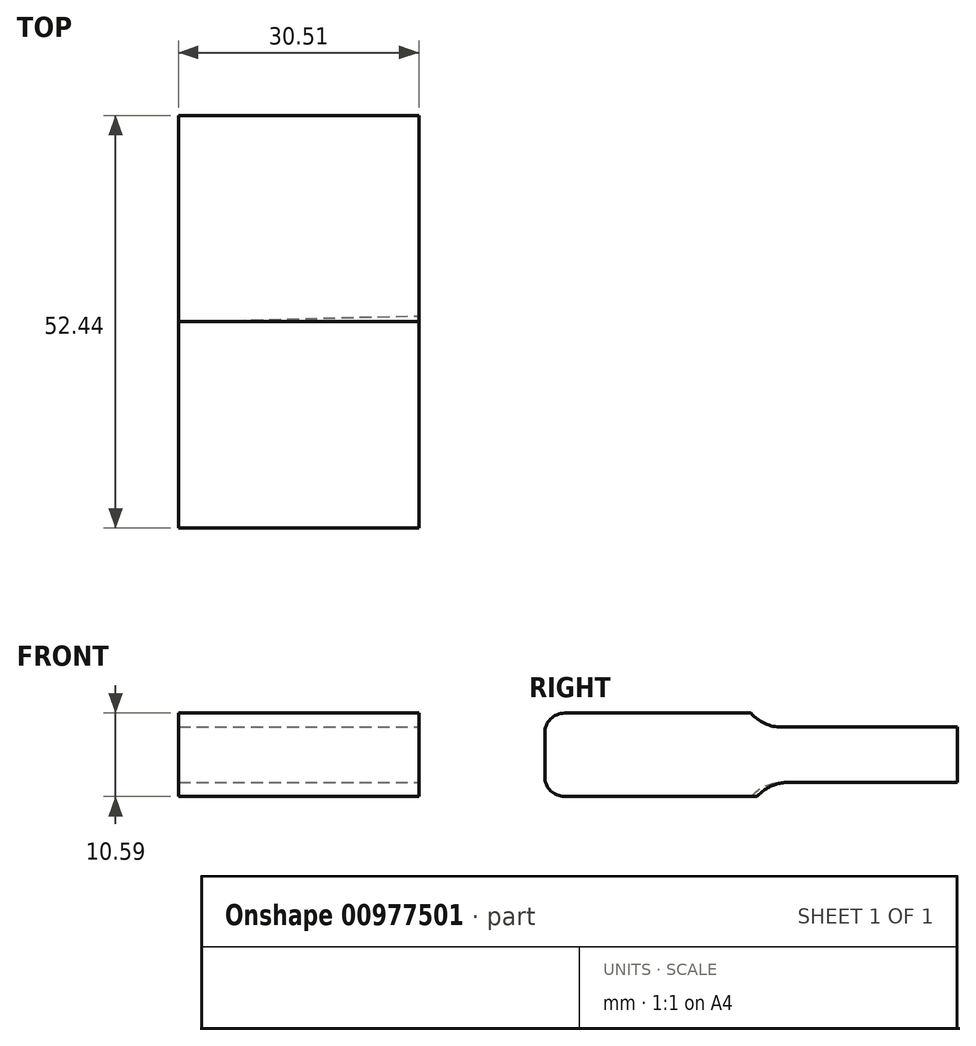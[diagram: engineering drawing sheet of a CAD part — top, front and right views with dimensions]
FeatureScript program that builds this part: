
annotation { "Feature Type Name" : "Feature", "Feature Type Description" : "" }
export const myFeature = defineFeature(function(context is Context, id is Id, definition is map)
    precondition{}
    {
        {
            var Q0;
            Q0=qCreatedBy(makeId("Top.planeOp"),FACE);
            var sketch = newSketch(context, id + "F0", { "sketchPlane" : qUnion([Q0])});
            skLineSegment(sketch, "E0", {"start": v(0, 0) * mm, "end": v(0, 52.44) * mm});
            skLineSegment(sketch, "E1", {"start": v(0, 52.44) * mm, "end": v(30.5, 52.44) * mm});
            skLineSegment(sketch, "E2", {"start": v(30.5, 52.44) * mm, "end": v(30.5, 0) * mm});
            skLineSegment(sketch, "E3", {"start": v(30.5, 0) * mm, "end": v(0, 0) * mm});
            skSolve(sketch);
        }
        {
            var Q0;
            Q0 = qSketchRegion(id + "F0", true);
            extrude(context, id + "F1", {"entities" : qUnion([Q0]), "depth" : 10.6 * mm, "offsetDistance" : 25.4 * mm});
        }
        {
            var Q0;
            Q0=makeQuery(id+"F1.opExtrude","CAP_FACE",FACE,{"disambiguationData":[OSD([sQuery(id+"F0.wireOp",EDGE,"E0"),sQuery(id+"F0.wireOp",EDGE,"E1"),sQuery(id+"F0.wireOp",EDGE,"E2"),sQuery(id+"F0.wireOp",EDGE,"E3")])],"isStart":false});
            var sketch = newSketch(context, id + "F2", { "sketchPlane" : qUnion([Q0])});
            skPoint(sketch, "E4.firstSnap0", {"position": v(0.74, 51.7) * mm});
            skLineSegment(sketch, "E5", {"start": v(0, 52.5) * mm, "end": v(0, 27.8) * mm});
            skLineSegment(sketch, "E6", {"start": v(0, 52.5) * mm, "end": v(30.5, 52.44) * mm});
            skLineSegment(sketch, "E7", {"start": v(30.5, 52.44) * mm, "end": v(30.5, 26.22) * mm});
            skLineSegment(sketch, "E8", {"start": v(30.5, 26.22) * mm, "end": v(0, 26.22) * mm});
            skSolve(sketch);
        }
        {
            var Q0;
            {var subQ7=sQuery(id+"F2.wireOp",EDGE,"E8");Q0=makeQuery(id+"F2.imprint","IMPRINT",FACE,{"disambiguationData":[TD([[makeQuery(id+"F2.imprint","IMPRINT",EDGE,{"derivedFrom":subQ7}),-1.0]])]});}
            extrude(context, id + "F3", {"entities" : qUnion([Q0]), "operationType" : NewBodyOperationType.REMOVE, "oppositeDirection" : true, "depth" : 1.78 * mm, "offsetDistance" : 25.4 * mm});
        }
        {
            var Q0;
            Q0=makeQuery(id+"F1.opExtrude","CAP_FACE",FACE,{"disambiguationData":[OSD([sQuery(id+"F0.wireOp",EDGE,"E0"),sQuery(id+"F0.wireOp",EDGE,"E1"),sQuery(id+"F0.wireOp",EDGE,"E2"),sQuery(id+"F0.wireOp",EDGE,"E3")])],"isStart":true});
            var sketch = newSketch(context, id + "F4", { "sketchPlane" : qUnion([Q0])});
            skLineSegment(sketch, "E9", {"start": v(0, -26.22) * mm, "end": v(30.5, -26.98) * mm});
            skLineSegment(sketch, "E10", {"start": v(30.5, -26.98) * mm, "end": v(30.5, -52.44) * mm});
            skLineSegment(sketch, "E11", {"start": v(30.5, -52.44) * mm, "end": v(0, -52.44) * mm});
            skLineSegment(sketch, "E12", {"start": v(0, -52.44) * mm, "end": v(0, -26.22) * mm});
            skSolve(sketch);
        }
        {
            var Q0;
            Q0 = qSketchRegion(id + "F4", true);
            extrude(context, id + "F5", {"entities" : qUnion([Q0]), "operationType" : NewBodyOperationType.REMOVE, "oppositeDirection" : true, "depth" : 1.78 * mm, "offsetDistance" : 25.4 * mm});
        }
        {
            var Q0;
            Q0=makeQuery(id+"F3.boolean.opBoolean","COPY",EDGE,{"derivedFrom":makeQuery(id+"F3.opExtrude","CAP_EDGE",EDGE,{"disambiguationData":[OSD([sQuery(id+"F2.wireOp",EDGE,"E8")])],"isStart":false})});
            var Q1;
            Q1=makeQuery(id+"F5.boolean.opBoolean","COPY",EDGE,{"derivedFrom":makeQuery(id+"F5.opExtrude","CAP_EDGE",EDGE,{"disambiguationData":[OSD([sQuery(id+"F4.wireOp",EDGE,"E9")])],"isStart":false})});
            fillet(context, id + "F6", {"entities" : qUnion([Q0, Q1]), "radius" : 5.08 * mm, "tangentPropagation" : true, "allowEdgeOverflow" : false});
        }
        {
            var Q0;
            Q0=makeQuery(id+"F5.boolean.opBoolean","COPY",EDGE,{"derivedFrom":makeQuery(id+"F5.opExtrude","CAP_EDGE",EDGE,{"disambiguationData":[OSD([sQuery(id+"F4.wireOp",EDGE,"E11")])],"isStart":false})});
            var Q1;
            Q1=makeQuery(id+"F3.boolean.opBoolean","MERGE",EDGE,{"derivedFrom":[],"fromTools":[makeQuery(id+"F3.opExtrude","CAP_EDGE",EDGE,{"disambiguationData":[OSD([sQuery(id+"F2.wireOp",EDGE,"E6")])],"isStart":false}),makeQuery(id+"F3.opExtrude","CAP_EDGE",EDGE,{"disambiguationData":[OSD([sQuery(id+"F0.wireOp",EDGE,"E1")])],"isStart":false})]});
            var Q2;
            Q2=makeQuery(id+"F1.opExtrude","CAP_EDGE",EDGE,{"disambiguationData":[OSD([sQuery(id+"F0.wireOp",EDGE,"E3")])],"isStart":true});
            var Q3;
            Q3=makeQuery(id+"F1.opExtrude","CAP_EDGE",EDGE,{"disambiguationData":[OSD([sQuery(id+"F0.wireOp",EDGE,"E3")])],"isStart":false});
            fillet(context, id + "F7", {"entities" : qUnion([Q0, Q1, Q2, Q3]), "radius" : 2.54 * mm, "tangentPropagation" : true, "allowEdgeOverflow" : false});
        }
    });
